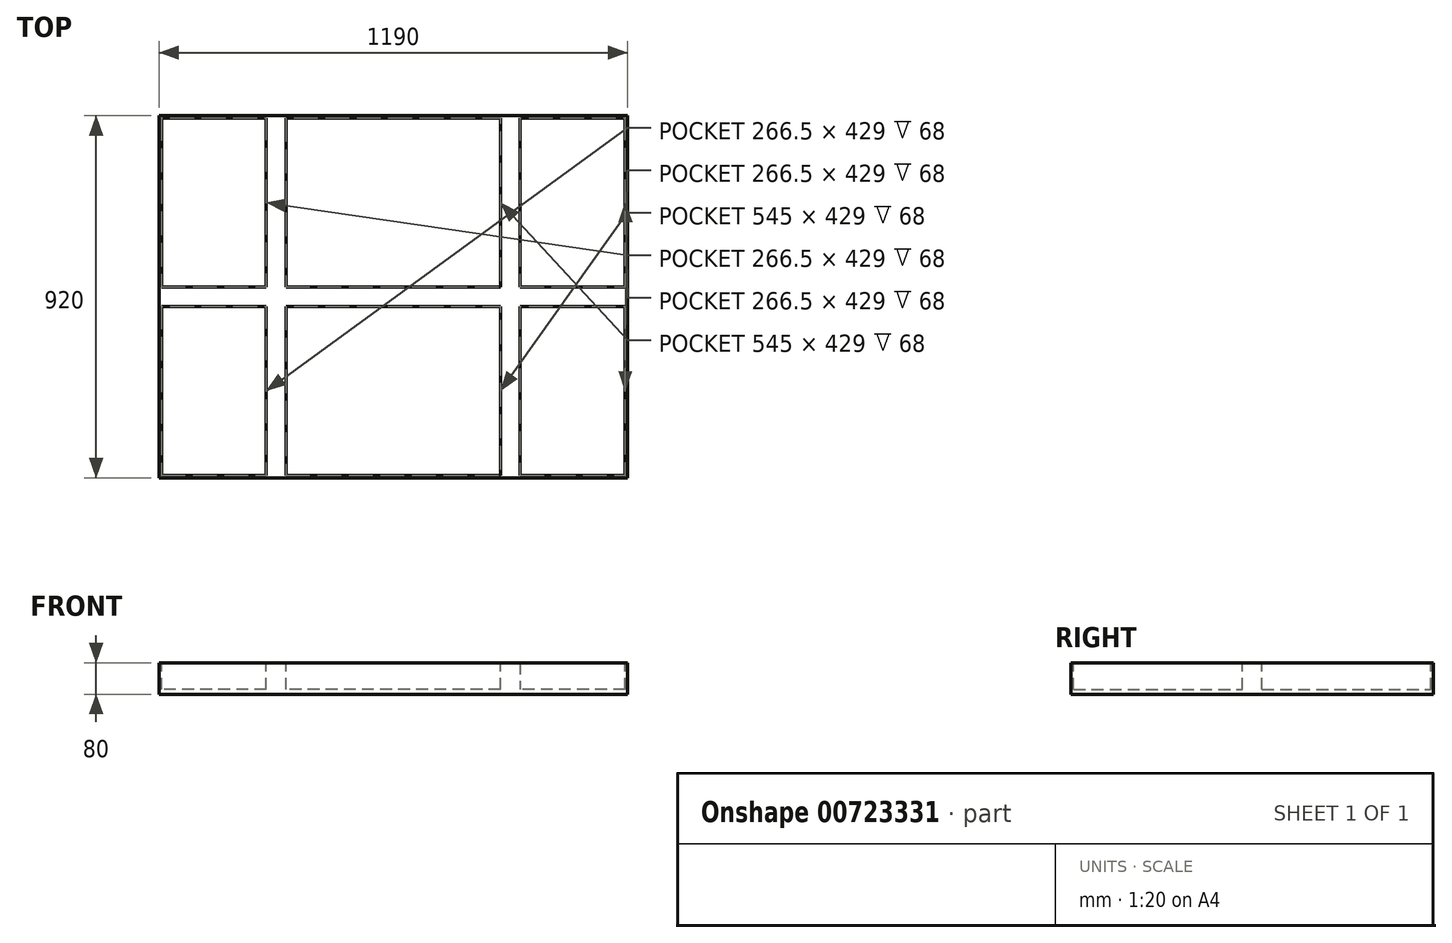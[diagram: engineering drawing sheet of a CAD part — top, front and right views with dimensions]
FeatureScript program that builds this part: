
annotation { "Feature Type Name" : "Feature", "Feature Type Description" : "" }
export const myFeature = defineFeature(function(context is Context, id is Id, definition is map)
    precondition{}
    {
        {
            var Q0;
            Q0=qCreatedBy(makeId("Top.planeOp"),FACE);
            var sketch = newSketch(context, id + "F0", { "sketchPlane" : qUnion([Q0])});
            skLineSegment(sketch, "E0.bottom", {"start": v(595, -460) * mm, "end": v(-595, -460) * mm});
            skLineSegment(sketch, "E0.top", {"start": v(595, 460) * mm, "end": v(-595, 460) * mm});
            skLineSegment(sketch, "E0.left", {"start": v(595, -460) * mm, "end": v(595, 460) * mm});
            skLineSegment(sketch, "E0.right", {"start": v(-595, -460) * mm, "end": v(-595, 460) * mm});
            skPoint(sketch, "E0.middle", {"position": v(0, 0) * mm});
            skSolve(sketch);
        }
        {
            var Q0;
            Q0=makeQuery(id+"F0.imprint","IMPRINT",FACE,{"disambiguationData":[TD([[makeQuery(id+"F0.imprint","IMPRINT",EDGE,{"derivedFrom":sQuery(id+"F0.wireOp",EDGE,"E0.bottom")}),-1.0]])]});
            extrude(context, id + "F1", {"entities" : qUnion([Q0]), "depth" : 80 * mm, "offsetDistance" : 25 * mm});
        }
        {
            var Q0;
            Q0=makeQuery(id+"F1.opExtrude","CAP_FACE",FACE,{"disambiguationData":[OSD([sQuery(id+"F0.wireOp",EDGE,"E0.bottom"),sQuery(id+"F0.wireOp",EDGE,"E0.top"),sQuery(id+"F0.wireOp",EDGE,"E0.left"),sQuery(id+"F0.wireOp",EDGE,"E0.right")])],"isStart":false});
            var sketch = newSketch(context, id + "F2", { "sketchPlane" : qUnion([Q0])});
            skLineSegment(sketch, "E1.bottom", {"start": v(589, -454) * mm, "end": v(-589, -454) * mm});
            skLineSegment(sketch, "E1.top", {"start": v(589, 454) * mm, "end": v(-589, 454) * mm});
            skLineSegment(sketch, "E1.left", {"start": v(589, -454) * mm, "end": v(589, 454) * mm});
            skLineSegment(sketch, "E1.right", {"start": v(-589, -454) * mm, "end": v(-589, 454) * mm});
            skPoint(sketch, "E1.middle", {"position": v(0, 0) * mm});
            skSolve(sketch);
        }
        {
            var Q0;
            Q0 = qSketchRegion(id + "F2", true);
            extrude(context, id + "F3", {"entities" : qUnion([Q0]), "operationType" : NewBodyOperationType.REMOVE, "oppositeDirection" : true, "depth" : 68 * mm, "offsetDistance" : 25 * mm});
        }
        {
            var Q0;
            Q0=makeQuery(id+"F3.boolean.opBoolean","COPY",FACE,{"derivedFrom":makeQuery(id+"F3.opExtrude","SWEPT_FACE",FACE,{"disambiguationData":[OSD([sQuery(id+"F2.wireOp",EDGE,"E1.bottom")])]})});
            var sketch = newSketch(context, id + "F4", { "sketchPlane" : qUnion([Q0])});
            skLineSegment(sketch, "E2", {"start": v(0, 80) * mm, "end": v(0, 0) * mm, "construction": true});
            skLineSegment(sketch, "E3.bottom", {"start": v(-272.5, 0) * mm, "end": v(-322.5, 0) * mm});
            skLineSegment(sketch, "E3.top", {"start": v(-272.5, 80) * mm, "end": v(-322.5, 80) * mm});
            skLineSegment(sketch, "E3.left", {"start": v(-272.5, 0) * mm, "end": v(-272.5, 80) * mm});
            skPoint(sketch, "E3.middle", {"position": v(-297.5, 40) * mm});
            skPoint(sketch, "E3.middle.positionSnap0", {"position": v(0, 40) * mm});
            skPoint(sketch, "E3.centerSnap0", {"position": v(0, 40) * mm});
            skLineSegment(sketch, "E4.MirrorCS", {"start": v(272.5, 80) * mm, "end": v(322.5, 80) * mm});
            skLineSegment(sketch, "E5.MirrorCS", {"start": v(272.5, 0) * mm, "end": v(322.5, 0) * mm});
            skLineSegment(sketch, "E6.MirrorCS", {"start": v(322.5, 0) * mm, "end": v(322.5, 80) * mm});
            skLineSegment(sketch, "E7.MirrorCS", {"start": v(272.5, 0) * mm, "end": v(272.5, 80) * mm});
            skLineSegment(sketch, "E8", {"start": v(-322.5, 80) * mm, "end": v(-322.5, 0) * mm});
            skSolve(sketch);
        }
        {
            var Q0;
            Q0 = qSketchRegion(id + "F4", true);
            extrude(context, id + "F5", {"entities" : qUnion([Q0]), "operationType" : NewBodyOperationType.ADD, "depth" : 908 * mm, "offsetDistance" : 25 * mm});
        }
        {
            var Q0;
            Q0=makeQuery(id+"F3.boolean.opBoolean","COPY",FACE,{"derivedFrom":makeQuery(id+"F3.opExtrude","SWEPT_FACE",FACE,{"disambiguationData":[OSD([sQuery(id+"F2.wireOp",EDGE,"E1.left")])]})});
            var sketch = newSketch(context, id + "F6", { "sketchPlane" : qUnion([Q0])});
            skLineSegment(sketch, "E9", {"start": v(0, 0) * mm, "end": v(0, 80) * mm, "construction": true});
            skLineSegment(sketch, "E10.bottom", {"start": v(25, 0) * mm, "end": v(-25, 0) * mm});
            skLineSegment(sketch, "E10.top", {"start": v(25, 80) * mm, "end": v(-25, 80) * mm});
            skLineSegment(sketch, "E10.left", {"start": v(25, 0) * mm, "end": v(25, 80) * mm});
            skLineSegment(sketch, "E10.right", {"start": v(-25, 0) * mm, "end": v(-25, 80) * mm});
            skPoint(sketch, "E10.middle", {"position": v(0, 40) * mm});
            skSolve(sketch);
        }
        {
            var Q0;
            Q0 = qSketchRegion(id + "F6", true);
            extrude(context, id + "F7", {"entities" : qUnion([Q0]), "operationType" : NewBodyOperationType.ADD, "depth" : 1178 * mm, "offsetDistance" : 25 * mm});
        }
    });
